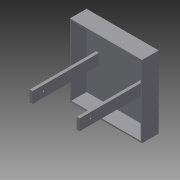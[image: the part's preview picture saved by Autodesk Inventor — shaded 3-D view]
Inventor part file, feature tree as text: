
AUTODESK INVENTOR PART (.ipt)
format: ipt  version: 2014 (Build 180170000, 170)  size: 132,608 bytes
history: native  units: in
note: dims shown in document units (in); Inventor stores cm internally (conversion verified against a paired STEP export)
features: extrude x7, sketch x6, projected_geometry x2, hole x1
ambient origin geometry x8: Origin, YZ Plane, XZ Plane, XY Plane, X Axis, Y Axis, Z Axis, Center Point
bodies: Solid1 (feature_tree)
feature tree (16):
  extrude  "Extrusion1"  Depth=26.0in
  sketch  "Sketch2"  dims[d2=6.0in d3=0.0in d6=3.0in d7=0.0in]
  extrude  "Extrusion2"  Depth=3.0in TaperAngle=0.0deg
  extrude  "Extrusion3"  Depth=3.0in TaperAngle=0.0deg
  sketch  "Sketch3"  dims[d8=2.0in d9=0.0in d10=3.0in d11=0.0in]
  extrude  "Extrusion4"  Depth=25.0in
  extrude  "Extrusion5"  Depth=5.5in TaperAngle=0.0deg
  extrude  "Extrusion6"  Depth=4.0in
  extrude  "Extrusion7"  Depth=24.0in TaperAngle=0.0deg
  hole  "Hole1"  [1 undecoded]
  sketch  "Sketch1"  dims[d0=26.0in d1=26.0in]
  projected_geometry  "Projected Loop1"
  projected_geometry  "Projected Loop2"
  sketch  "Sketch4"  dims[d12=2.0in d13=0.0in d14=25.0in]
  sketch  "Sketch5"  dims[d15=25.0in d16=5.5in d17=0.0in]
  sketch  "Sketch6"  dims[d19=1.0in d20=4.0in d21=24.0in d22=0.0in d23=4.0in d24=0.5in d25=0.75in d26=0.375in d27=0.25in d28=0.5635in d29=1.0in d30=0.8108in]
note: 1 required parameter value undecoded (feature->parameter linkage not recoverable at this tier; creation-order binding heuristic only, values carry confidence <= 0.55)
